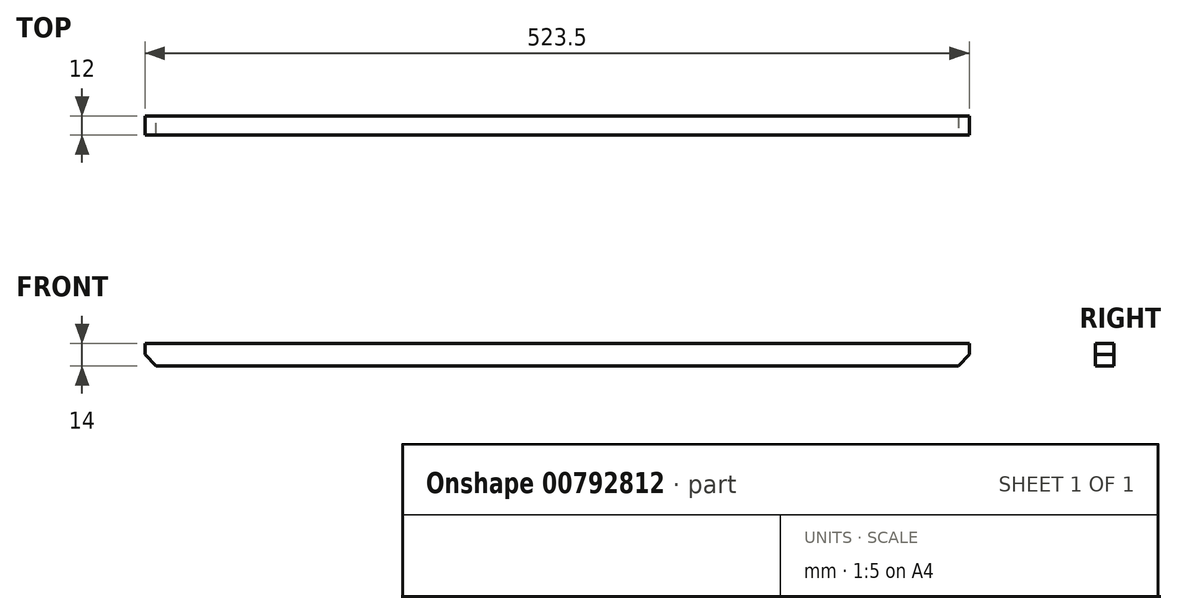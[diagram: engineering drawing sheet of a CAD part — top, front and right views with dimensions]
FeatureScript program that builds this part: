
annotation { "Feature Type Name" : "Feature", "Feature Type Description" : "" }
export const myFeature = defineFeature(function(context is Context, id is Id, definition is map)
    precondition{}
    {
        {
            var Q0;
            Q0=qCreatedBy(makeId("Front.planeOp"),FACE);
            var sketch = newSketch(context, id + "F0", { "sketchPlane" : qUnion([Q0])});
            skLineSegment(sketch, "E0.bottom", {"start": v(261.75, -7) * mm, "end": v(-261.75, -7) * mm});
            skLineSegment(sketch, "E0.top", {"start": v(261.75, 7) * mm, "end": v(-261.75, 7) * mm});
            skLineSegment(sketch, "E0.left", {"start": v(261.75, -7) * mm, "end": v(261.75, 7) * mm});
            skLineSegment(sketch, "E0.right", {"start": v(-261.75, -7) * mm, "end": v(-261.75, 7) * mm});
            skPoint(sketch, "E0.middle", {"position": v(0, 0) * mm});
            skSolve(sketch);
        }
        {
            var Q0;
            Q0 = qSketchRegion(id + "F0", true);
            extrude(context, id + "F1", {"entities" : qUnion([Q0]), "depth" : 12 * mm, "offsetDistance" : 25 * mm});
        }
        {
            var Q0;
            Q0=makeQuery(id+"F1.opExtrude","SWEPT_EDGE",EDGE,{"disambiguationData":[OSD([sQuery(id+"F0.wireOp",EDGE,"E0.bottom"),sQuery(id+"F0.wireOp",EDGE,"E0.left")])]});
            chamfer(context, id + "F2", {"entities" : qUnion([Q0]), "width" : 7 * mm, "tangentPropagation" : true});
        }
        {
            var Q0;
            Q0=makeQuery(id+"F1.opExtrude","SWEPT_EDGE",EDGE,{"disambiguationData":[OSD([sQuery(id+"F0.wireOp",EDGE,"E0.bottom"),sQuery(id+"F0.wireOp",EDGE,"E0.right")])]});
            chamfer(context, id + "F3", {"entities" : qUnion([Q0]), "width" : 7 * mm, "tangentPropagation" : true});
        }
    });
